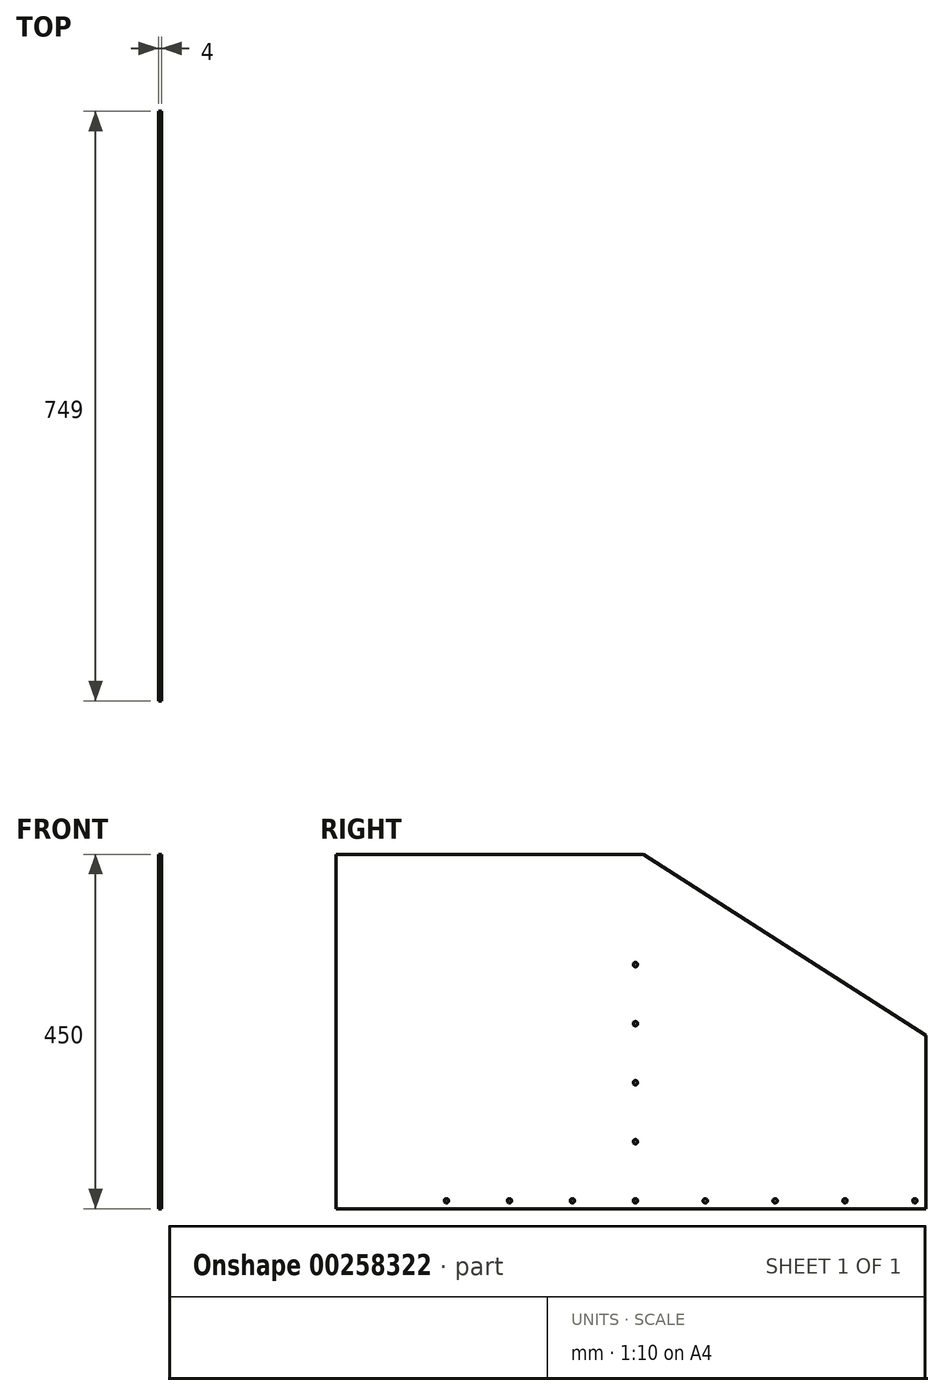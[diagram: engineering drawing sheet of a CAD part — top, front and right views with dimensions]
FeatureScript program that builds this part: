
annotation { "Feature Type Name" : "Feature", "Feature Type Description" : "" }
export const myFeature = defineFeature(function(context is Context, id is Id, definition is map)
    precondition{}
    {
        {
            var Q0;
            Q0=qCreatedBy(makeId("Right.planeOp"),FACE);
            var sketch = newSketch(context, id + "F0", { "sketchPlane" : qUnion([Q0])});
            skLineSegment(sketch, "E0", {"start": v(0, 0) * mm, "end": v(0, 320) * mm, "construction": true});
            skLineSegment(sketch, "E1", {"start": v(379, 0) * mm, "end": v(0, 0) * mm});
            skLineSegment(sketch, "E2", {"start": v(0, 320) * mm, "end": v(20, 320) * mm, "construction": true});
            skLineSegment(sketch, "E3", {"start": v(20, 320) * mm, "end": v(379, 26) * mm, "construction": true});
            skLineSegment(sketch, "E4", {"start": v(379, 26) * mm, "end": v(379, 0) * mm, "construction": true});
            skCircle(sketch, "E5", {"center": v(365, 10) * mm, "radius": 2.75 * mm});
            skCircle(sketch, "E6", {"center": v(276.25, 10) * mm, "radius": 2.75 * mm});
            skCircle(sketch, "E7", {"center": v(187.5, 10) * mm, "radius": 2.75 * mm});
            skCircle(sketch, "E8", {"center": v(98.75, 10) * mm, "radius": 2.75 * mm});
            skCircle(sketch, "E9", {"center": v(10, 10) * mm, "radius": 2.75 * mm});
            skCircle(sketch, "E10", {"center": v(10, 85) * mm, "radius": 2.75 * mm});
            skCircle(sketch, "E11", {"center": v(10, 160) * mm, "radius": 2.75 * mm});
            skCircle(sketch, "E12", {"center": v(10, 235) * mm, "radius": 2.75 * mm});
            skCircle(sketch, "E13", {"center": v(10, 310) * mm, "radius": 2.75 * mm});
            skLineSegment(sketch, "E14", {"start": v(10, 310) * mm, "end": v(10, 235) * mm, "construction": true});
            skLineSegment(sketch, "E15", {"start": v(10, 235) * mm, "end": v(10, 160) * mm, "construction": true});
            skLineSegment(sketch, "E16", {"start": v(10, 160) * mm, "end": v(10, 85) * mm, "construction": true});
            skLineSegment(sketch, "E17", {"start": v(10, 85) * mm, "end": v(10, 10) * mm, "construction": true});
            skLineSegment(sketch, "E18", {"start": v(10, 10) * mm, "end": v(98.75, 10) * mm, "construction": true});
            skLineSegment(sketch, "E19", {"start": v(98.75, 10) * mm, "end": v(187.5, 10) * mm, "construction": true});
            skLineSegment(sketch, "E20", {"start": v(187.5, 10) * mm, "end": v(276.25, 10) * mm, "construction": true});
            skLineSegment(sketch, "E21", {"start": v(276.25, 10) * mm, "end": v(365, 10) * mm, "construction": true});
            skLineSegment(sketch, "E22", {"start": v(365, 10) * mm, "end": v(379, 10) * mm, "construction": true});
            skLineSegment(sketch, "E23", {"start": v(10, 10) * mm, "end": v(10, 0) * mm, "construction": true});
            skLineSegment(sketch, "E24", {"start": v(10, 310) * mm, "end": v(10, 320) * mm, "construction": true});
            skLineSegment(sketch, "E25", {"start": v(379, 0) * mm, "end": v(379, 220) * mm});
            skLineSegment(sketch, "E26", {"start": v(0, 450) * mm, "end": v(0, 0) * mm, "construction": true});
            skLineSegment(sketch, "E27", {"start": v(0, 450) * mm, "end": v(20, 450) * mm});
            skLineSegment(sketch, "E28", {"start": v(20, 450) * mm, "end": v(379, 220) * mm});
            skLineSegment(sketch, "E29", {"start": v(0, 0) * mm, "end": v(-370, 0) * mm});
            skLineSegment(sketch, "E30", {"start": v(-370, 0) * mm, "end": v(-370, 450) * mm});
            skLineSegment(sketch, "E31", {"start": v(-370, 450) * mm, "end": v(0, 450) * mm});
            skCircle(sketch, "E32", {"center": v(-230, 10) * mm, "radius": 2.75 * mm});
            skCircle(sketch, "E33", {"center": v(-150, 10) * mm, "radius": 2.75 * mm});
            skCircle(sketch, "E34", {"center": v(-70, 10) * mm, "radius": 2.75 * mm});
            skLineSegment(sketch, "E35", {"start": v(10, 10) * mm, "end": v(-70, 10) * mm, "construction": true});
            skLineSegment(sketch, "E36", {"start": v(-70, 10) * mm, "end": v(-150, 10) * mm, "construction": true});
            skLineSegment(sketch, "E37", {"start": v(-150, 10) * mm, "end": v(-230, 10) * mm, "construction": true});
            skSolve(sketch);
        }
        {
            var Q0;
            Q0 = qSketchRegion(id + "F0", true);
            extrude(context, id + "F1", {"entities" : qUnion([Q0]), "depth" : 4 * mm});
        }
    });
